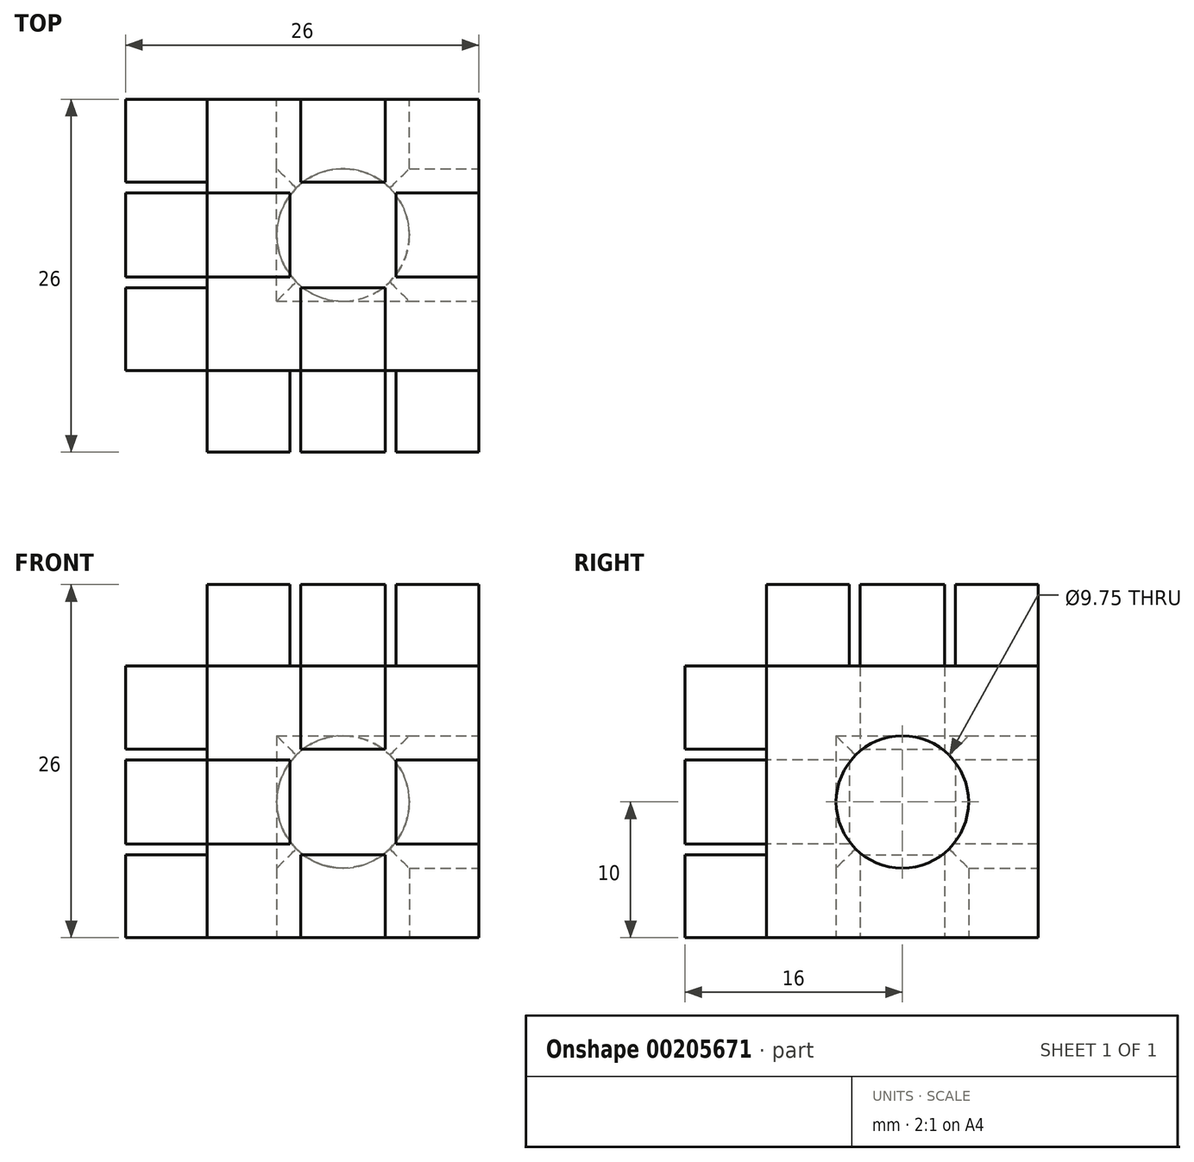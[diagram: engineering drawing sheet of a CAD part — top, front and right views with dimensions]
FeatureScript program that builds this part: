
annotation { "Feature Type Name" : "Feature", "Feature Type Description" : "" }
export const myFeature = defineFeature(function(context is Context, id is Id, definition is map)
    precondition{}
    {
        {
            assignVariable(context, id + "F0", {"name" : "cut_depth", "anyValue" : (10 + 9.75 / 2)});
        }
        {
            var Q0;
            Q0=qCreatedBy(makeId("Top.planeOp"),FACE);
            var sketch = newSketch(context, id + "F1", { "sketchPlane" : qUnion([Q0])});
            skLineSegment(sketch, "E0.bottom", {"start": v(10, 10) * mm, "end": v(-10, 10) * mm});
            skLineSegment(sketch, "E0.top", {"start": v(10, -10) * mm, "end": v(-10, -10) * mm});
            skLineSegment(sketch, "E0.left", {"start": v(10, 10) * mm, "end": v(10, -10) * mm});
            skLineSegment(sketch, "E0.right", {"start": v(-10, 10) * mm, "end": v(-10, -10) * mm});
            skPoint(sketch, "E0.middle", {"position": v(0, 0) * mm});
            skSolve(sketch);
        }
        {
            var Q0;
            Q0=makeQuery(id+"F1.imprint","IMPRINT",FACE,{"disambiguationData":[TD([[makeQuery(id+"F1.imprint","IMPRINT",EDGE,{"derivedFrom":sQuery(id+"F1.wireOp",EDGE,"E0.bottom")}),1.0]])]});
            extrude(context, id + "F2", {"entities" : qUnion([Q0]), "depth" : 20 * mm});
        }
        {
            var Q0;
            Q0=makeQuery(id+"F2.opExtrude","CAP_FACE",FACE,{"disambiguationData":[OSD([sQuery(id+"F1.wireOp",EDGE,"E0.bottom"),sQuery(id+"F1.wireOp",EDGE,"E0.top"),sQuery(id+"F1.wireOp",EDGE,"E0.left"),sQuery(id+"F1.wireOp",EDGE,"E0.right")])],"isStart":false});
            var sketch = newSketch(context, id + "F3", { "sketchPlane" : qUnion([Q0])});
            skLineSegment(sketch, "E1.bottom", {"start": v(-3.9, -3.1) * mm, "end": v(-10, -3.1) * mm});
            skLineSegment(sketch, "E1.top", {"start": v(-3.9, 3.1) * mm, "end": v(-10, 3.1) * mm});
            skLineSegment(sketch, "E1.left", {"start": v(-3.9, -3.1) * mm, "end": v(-3.9, 3.1) * mm});
            skLineSegment(sketch, "E1.right", {"start": v(-10, -3.1) * mm, "end": v(-10, 3.1) * mm});
            skPoint(sketch, "E1.middle", {"position": v(-6.95, 0) * mm});
            skLineSegment(sketch, "E2.bottom", {"start": v(10, -3.1) * mm, "end": v(3.9, -3.1) * mm});
            skLineSegment(sketch, "E2.top", {"start": v(10, 3.1) * mm, "end": v(3.9, 3.1) * mm});
            skLineSegment(sketch, "E2.left", {"start": v(10, -3.1) * mm, "end": v(10, 3.1) * mm});
            skLineSegment(sketch, "E2.right", {"start": v(3.9, -3.1) * mm, "end": v(3.9, 3.1) * mm});
            skPoint(sketch, "E2.middle", {"position": v(6.95, 0) * mm});
            skLineSegment(sketch, "E3.bottom", {"start": v(3.1, 10) * mm, "end": v(-3.1, 10) * mm});
            skLineSegment(sketch, "E3.top", {"start": v(3.1, 3.9) * mm, "end": v(-3.1, 3.9) * mm});
            skLineSegment(sketch, "E3.left", {"start": v(3.1, 10) * mm, "end": v(3.1, 3.9) * mm});
            skLineSegment(sketch, "E3.right", {"start": v(-3.1, 10) * mm, "end": v(-3.1, 3.9) * mm});
            skPoint(sketch, "E3.middle", {"position": v(0, 6.95) * mm});
            skLineSegment(sketch, "E4.bottom", {"start": v(3.1, -3.9) * mm, "end": v(-3.1, -3.9) * mm});
            skLineSegment(sketch, "E4.top", {"start": v(3.1, -10) * mm, "end": v(-3.1, -10) * mm});
            skLineSegment(sketch, "E4.left", {"start": v(3.1, -3.9) * mm, "end": v(3.1, -10) * mm});
            skLineSegment(sketch, "E4.right", {"start": v(-3.1, -3.9) * mm, "end": v(-3.1, -10) * mm});
            skPoint(sketch, "E4.middle", {"position": v(0, -6.95) * mm});
            skLineSegment(sketch, "E5.bottom", {"start": v(6.95, -6.95) * mm, "end": v(-6.95, -6.95) * mm, "construction": true});
            skLineSegment(sketch, "E5.top", {"start": v(6.95, 6.95) * mm, "end": v(-6.95, 6.95) * mm, "construction": true});
            skLineSegment(sketch, "E5.left", {"start": v(6.95, -6.95) * mm, "end": v(6.95, 6.95) * mm, "construction": true});
            skLineSegment(sketch, "E5.right", {"start": v(-6.95, -6.95) * mm, "end": v(-6.95, 6.95) * mm, "construction": true});
            skPoint(sketch, "E5.middle", {"position": v(0, 0) * mm});
            skLineSegment(sketch, "E6.bottom", {"start": v(3.9, 3.9) * mm, "end": v(-3.9, 3.9) * mm, "construction": true});
            skLineSegment(sketch, "E6.top", {"start": v(3.9, -3.9) * mm, "end": v(-3.9, -3.9) * mm, "construction": true});
            skLineSegment(sketch, "E6.left", {"start": v(3.9, 3.9) * mm, "end": v(3.9, -3.9) * mm, "construction": true});
            skLineSegment(sketch, "E6.right", {"start": v(-3.9, 3.9) * mm, "end": v(-3.9, -3.9) * mm, "construction": true});
            skSolve(sketch);
        }
        {
            var Q0;
            Q0=makeQuery(id+"F3.imprint","IMPRINT",FACE,{"disambiguationData":[TD([[makeQuery(id+"F3.imprint","IMPRINT",EDGE,{"derivedFrom":sQuery(id+"F3.wireOp",EDGE,"E3.bottom")}),1.0]])]});
            var Q1;
            Q1=makeQuery(id+"F3.imprint","IMPRINT",FACE,{"disambiguationData":[TD([[makeQuery(id+"F3.imprint","IMPRINT",EDGE,{"derivedFrom":sQuery(id+"F3.wireOp",EDGE,"E1.bottom")}),-1.0]])]});
            var Q2;
            Q2=makeQuery(id+"F3.imprint","IMPRINT",FACE,{"disambiguationData":[TD([[makeQuery(id+"F3.imprint","IMPRINT",EDGE,{"derivedFrom":sQuery(id+"F3.wireOp",EDGE,"E4.bottom")}),1.0]])]});
            var Q3;
            Q3=makeQuery(id+"F3.imprint","IMPRINT",FACE,{"disambiguationData":[TD([[makeQuery(id+"F3.imprint","IMPRINT",EDGE,{"derivedFrom":sQuery(id+"F3.wireOp",EDGE,"E2.bottom")}),-1.0]])]});
            extrude(context, id + "F4", {"entities" : qUnion([Q0, Q1, Q2, Q3]), "depth" : 6 * mm});
        }
        {
            var Q0;
            Q0=makeQuery(id+"F2.opExtrude","SWEPT_EDGE",EDGE,{"disambiguationData":[OSD([sQuery(id+"F1.wireOp",EDGE,"E0.top"),sQuery(id+"F1.wireOp",EDGE,"E0.right")])]});
            cPoint(context, id + "F5", {"entities" : qUnion([Q0]), "parameter" : 0.5});
        }
        {
            var Q0;
            Q0=makeQuery(id+"F2.opExtrude","SWEPT_EDGE",EDGE,{"disambiguationData":[OSD([sQuery(id+"F1.wireOp",EDGE,"E0.bottom"),sQuery(id+"F1.wireOp",EDGE,"E0.right")])]});
            cPoint(context, id + "F6", {"entities" : qUnion([Q0]), "parameter" : 0.5});
        }
        {
            var Q0;
            Q0=makeQuery(id+"F2.opExtrude","SWEPT_EDGE",EDGE,{"disambiguationData":[OSD([sQuery(id+"F1.wireOp",EDGE,"E0.bottom"),sQuery(id+"F1.wireOp",EDGE,"E0.left")])]});
            cPoint(context, id + "F7", {"entities" : qUnion([Q0]), "parameter" : 0.5});
        }
        {
            var Q0;
            Q0 = qCreatedBy(id + "F5" ,VERTEX);
            var Q1;
            Q1 = qCreatedBy(id + "F6" ,VERTEX);
            var Q2;
            Q2 = qCreatedBy(id + "F7" ,VERTEX);
            cPlane(context, id + "F8", {"entities" : qUnion([Q0, Q1, Q2]), "cplaneType" : CPlaneType.THREE_POINT, "offset" : 25 * mm, "width" : 150 * mm, "height" : 150 * mm});
        }
        {
            var Q0;
            Q0=qCreatedBy(id+"F8.planeOp",FACE);
            var sketch = newSketch(context, id + "F9", { "sketchPlane" : qUnion([Q0])});
            skPoint(sketch, "E7.0", {"position": v(-10, 0) * mm});
            skPoint(sketch, "E8.0", {"position": v(0, 10) * mm});
            skPoint(sketch, "E9.0", {"position": v(10, 0) * mm});
            skPoint(sketch, "E10.0", {"position": v(0, -10) * mm});
            skLineSegment(sketch, "E11", {"start": v(-10, 0) * mm, "end": v(10, 0) * mm, "construction": true});
            skLineSegment(sketch, "E12", {"start": v(0, 10) * mm, "end": v(0, -10) * mm, "construction": true});
            skSolve(sketch);
        }
        {
            var Q0;
            Q0=makeQuery(id+"F4.opExtrude","SWEPT_BODY",BODY,{"disambiguationData":[OSD([sQuery(id+"F3.wireOp",EDGE,"E3.bottom"),sQuery(id+"F3.wireOp",EDGE,"E3.top"),sQuery(id+"F3.wireOp",EDGE,"E3.left"),sQuery(id+"F3.wireOp",EDGE,"E3.right")])]});
            var Q1;
            Q1=makeQuery(id+"F4.opExtrude","SWEPT_BODY",BODY,{"disambiguationData":[OSD([sQuery(id+"F3.wireOp",EDGE,"E1.bottom"),sQuery(id+"F3.wireOp",EDGE,"E1.top"),sQuery(id+"F3.wireOp",EDGE,"E1.left"),sQuery(id+"F3.wireOp",EDGE,"E1.right")])]});
            var Q2;
            Q2=makeQuery(id+"F4.opExtrude","SWEPT_BODY",BODY,{"disambiguationData":[OSD([sQuery(id+"F3.wireOp",EDGE,"E2.bottom"),sQuery(id+"F3.wireOp",EDGE,"E2.top"),sQuery(id+"F3.wireOp",EDGE,"E2.left"),sQuery(id+"F3.wireOp",EDGE,"E2.right")])]});
            var Q3;
            Q3=makeQuery(id+"F4.opExtrude","SWEPT_BODY",BODY,{"disambiguationData":[OSD([sQuery(id+"F3.wireOp",EDGE,"E4.bottom"),sQuery(id+"F3.wireOp",EDGE,"E4.top"),sQuery(id+"F3.wireOp",EDGE,"E4.left"),sQuery(id+"F3.wireOp",EDGE,"E4.right")])]});
            var Q4;
            Q4=sQuery(id+"F9.wireOp",EDGE,"E12");
            circularPattern(context, id + "F10", {"entities" : qUnion([Q0, Q1, Q2, Q3]), "axis" : qUnion([Q4]), "angle" : 90 * degree, "instanceCount" : 2, "equalSpace" : true});
        }
        {
            var Q0;
            Q0=makeQuery(id+"F4.opExtrude","SWEPT_BODY",BODY,{"disambiguationData":[OSD([sQuery(id+"F3.wireOp",EDGE,"E3.bottom"),sQuery(id+"F3.wireOp",EDGE,"E3.top"),sQuery(id+"F3.wireOp",EDGE,"E3.left"),sQuery(id+"F3.wireOp",EDGE,"E3.right")])]});
            var Q1;
            Q1=makeQuery(id+"F4.opExtrude","SWEPT_BODY",BODY,{"disambiguationData":[OSD([sQuery(id+"F3.wireOp",EDGE,"E1.bottom"),sQuery(id+"F3.wireOp",EDGE,"E1.top"),sQuery(id+"F3.wireOp",EDGE,"E1.left"),sQuery(id+"F3.wireOp",EDGE,"E1.right")])]});
            var Q2;
            Q2=makeQuery(id+"F4.opExtrude","SWEPT_BODY",BODY,{"disambiguationData":[OSD([sQuery(id+"F3.wireOp",EDGE,"E4.bottom"),sQuery(id+"F3.wireOp",EDGE,"E4.top"),sQuery(id+"F3.wireOp",EDGE,"E4.left"),sQuery(id+"F3.wireOp",EDGE,"E4.right")])]});
            var Q3;
            Q3=makeQuery(id+"F4.opExtrude","SWEPT_BODY",BODY,{"disambiguationData":[OSD([sQuery(id+"F3.wireOp",EDGE,"E2.bottom"),sQuery(id+"F3.wireOp",EDGE,"E2.top"),sQuery(id+"F3.wireOp",EDGE,"E2.left"),sQuery(id+"F3.wireOp",EDGE,"E2.right")])]});
            var Q4;
            Q4=sQuery(id+"F9.wireOp",EDGE,"E11");
            circularPattern(context, id + "F11", {"entities" : qUnion([Q0, Q1, Q2, Q3]), "axis" : qUnion([Q4]), "angle" : 90 * degree, "instanceCount" : 2, "equalSpace" : true});
        }
        {
            var Q0;
            Q0=makeQuery(id+"F2.opExtrude","CAP_FACE",FACE,{"disambiguationData":[OSD([sQuery(id+"F1.wireOp",EDGE,"E0.bottom"),sQuery(id+"F1.wireOp",EDGE,"E0.top"),sQuery(id+"F1.wireOp",EDGE,"E0.left"),sQuery(id+"F1.wireOp",EDGE,"E0.right")])],"isStart":true});
            var sketch = newSketch(context, id + "F12", { "sketchPlane" : qUnion([Q0])});
            skCircle(sketch, "E13", {"center": v(0, 0) * mm, "radius": 4.88 * mm});
            skSolve(sketch);
        }
        {
            var Q0;
            Q0=makeQuery(id+"F2.opExtrude","SWEPT_FACE",FACE,{"disambiguationData":[OSD([sQuery(id+"F1.wireOp",EDGE,"E0.bottom")])]});
            var sketch = newSketch(context, id + "F13", { "sketchPlane" : qUnion([Q0])});
            skPoint(sketch, "E14.0", {"position": v(0, 10) * mm});
            skCircle(sketch, "E15", {"center": v(0, 10) * mm, "radius": 4.88 * mm});
            skSolve(sketch);
        }
        {
            var Q0;
            Q0=makeQuery(id+"F2.opExtrude","SWEPT_FACE",FACE,{"disambiguationData":[OSD([sQuery(id+"F1.wireOp",EDGE,"E0.left")])]});
            var sketch = newSketch(context, id + "F14", { "sketchPlane" : qUnion([Q0])});
            skPoint(sketch, "E16.0", {"position": v(0, 10) * mm});
            skCircle(sketch, "E17", {"center": v(0, 10) * mm, "radius": 4.88 * mm});
            skSolve(sketch);
        }
        {
            var Q0;
            Q0=makeQuery(id+"F13.imprint","IMPRINT",FACE,{"disambiguationData":[TD([[makeQuery(id+"F13.imprint","IMPRINT",EDGE,{"derivedFrom":sQuery(id+"F13.wireOp",EDGE,"E15")}),1.0]])]});
            extrude(context, id + "F15", {"entities" : qUnion([Q0]), "operationType" : NewBodyOperationType.REMOVE, "oppositeDirection" : true, "depth" : (getVariable(context, 'cut_depth')) * mm});
        }
        {
            var Q0;
            Q0=makeQuery(id+"F12.imprint","IMPRINT",FACE,{"disambiguationData":[TD([[makeQuery(id+"F12.imprint","IMPRINT",EDGE,{"derivedFrom":sQuery(id+"F12.wireOp",EDGE,"E13")}),1.0]])]});
            extrude(context, id + "F16", {"entities" : qUnion([Q0]), "operationType" : NewBodyOperationType.REMOVE, "oppositeDirection" : true, "depth" : (getVariable(context, 'cut_depth')) * mm});
        }
        {
            var Q0;
            Q0=makeQuery(id+"F14.imprint","IMPRINT",FACE,{"disambiguationData":[TD([[makeQuery(id+"F14.imprint","IMPRINT",EDGE,{"derivedFrom":sQuery(id+"F14.wireOp",EDGE,"E17")}),1.0]])]});
            extrude(context, id + "F17", {"entities" : qUnion([Q0]), "operationType" : NewBodyOperationType.REMOVE, "oppositeDirection" : true, "depth" : (getVariable(context, 'cut_depth')) * mm});
        }
        {
            var Q0;
            Q0=makeQuery(id+"F17.boolean.opBoolean","COPY",FACE,{"derivedFrom":makeQuery(id+"F17.opExtrude","CAP_FACE",FACE,{"disambiguationData":[OSD([sQuery(id+"F14.wireOp",EDGE,"E17")])],"isStart":false})});
            var sketch = newSketch(context, id + "F18", { "sketchPlane" : qUnion([Q0])});
            skPoint(sketch, "E18.0", {"position": v(0, 10) * mm});
            skSolve(sketch);
        }
        {
            var Q0;
            Q0=makeQuery(id+"F16.boolean.opBoolean","COPY",FACE,{"derivedFrom":makeQuery(id+"F16.opExtrude","CAP_FACE",FACE,{"disambiguationData":[OSD([sQuery(id+"F12.wireOp",EDGE,"E13")])],"isStart":false})});
            var sketch = newSketch(context, id + "F19", { "sketchPlane" : qUnion([Q0])});
            skPoint(sketch, "E19.0", {"position": v(0, 0) * mm});
            skSolve(sketch);
        }
        {
            var Q0;
            Q0=makeQuery(id+"F15.boolean.opBoolean","COPY",FACE,{"derivedFrom":makeQuery(id+"F15.opExtrude","CAP_FACE",FACE,{"disambiguationData":[OSD([sQuery(id+"F13.wireOp",EDGE,"E15")])],"isStart":false})});
            var sketch = newSketch(context, id + "F20", { "sketchPlane" : qUnion([Q0])});
            skPoint(sketch, "E20.0", {"position": v(0, 10) * mm});
            skSolve(sketch);
        }
        {
            var Q0;
            Q0=sQuery(id+"F20.wireOp",VERTEX,"E20.0");
            var Q1;
            Q1=sQuery(id+"F19.wireOp",VERTEX,"E19.0");
            var Q2;
            Q2=sQuery(id+"F18.wireOp",VERTEX,"E18.0");
            var Q3;
            Q3=makeQuery(id+"F4.opExtrude","SWEPT_BODY",BODY,{"disambiguationData":[OSD([sQuery(id+"F3.wireOp",EDGE,"E3.bottom"),sQuery(id+"F3.wireOp",EDGE,"E3.top"),sQuery(id+"F3.wireOp",EDGE,"E3.left"),sQuery(id+"F3.wireOp",EDGE,"E3.right")])]});
            hole(context, id + "F21", {"style" : HoleStyle.C_BORE, "endStyle" : HoleEndStyle.BLIND, "holeDiameter" : 5.5 * mm, "cBoreDiameter" : 9.75 * mm, "cBoreDepth" : 1.8 * mm, "holeDepth" : 20 * mm, "locations" : qUnion([Q0, Q1, Q2]), "scope" : qUnion([Q3])});
        }
    });
